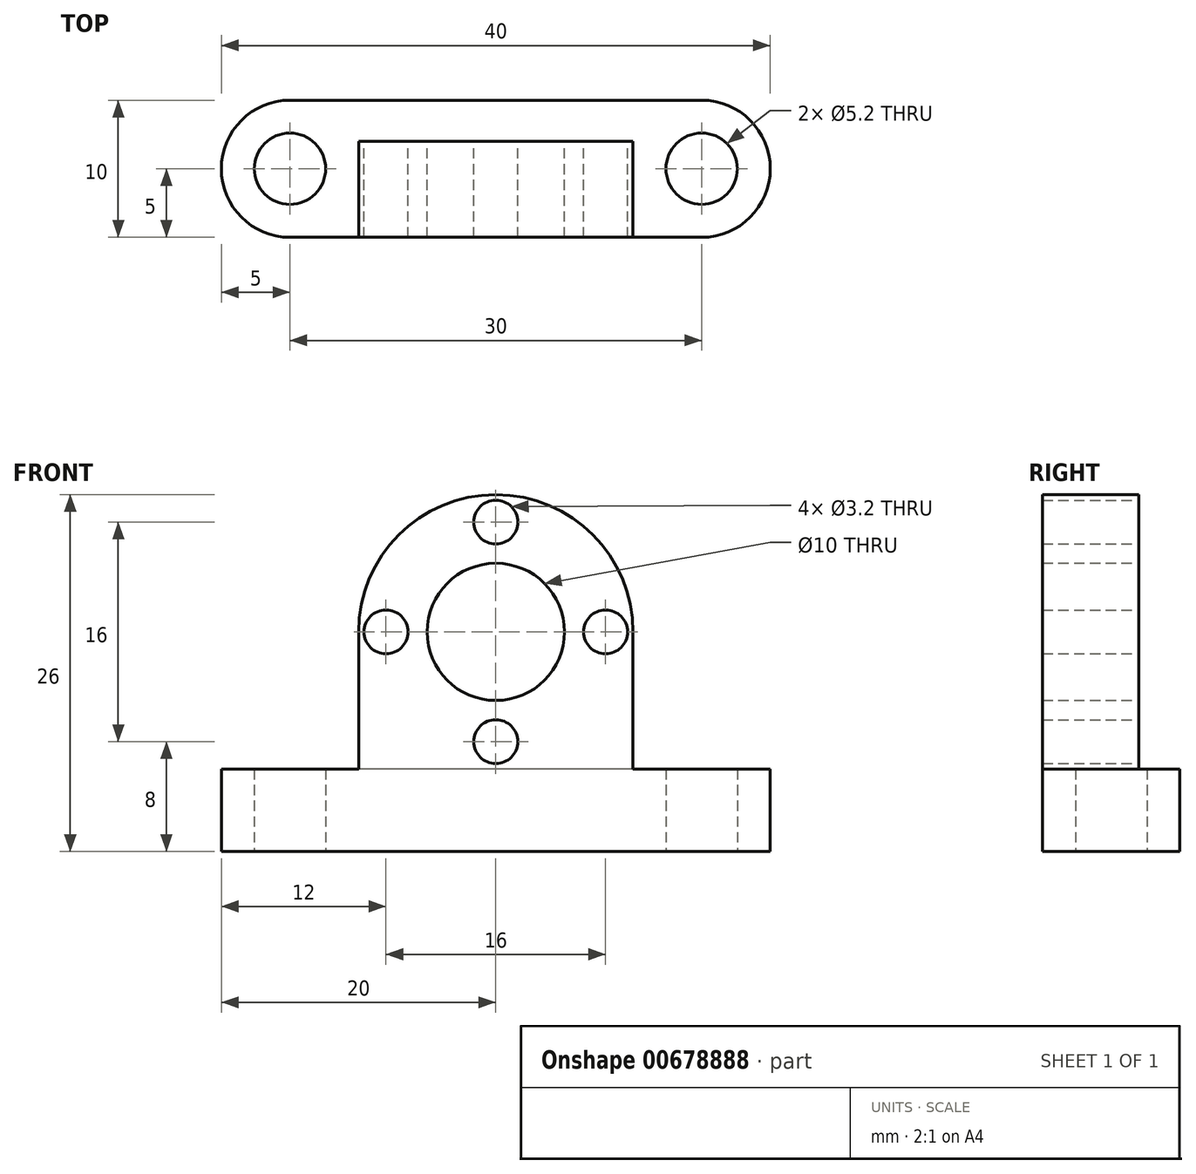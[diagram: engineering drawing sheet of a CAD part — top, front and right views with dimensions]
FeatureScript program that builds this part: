
annotation { "Feature Type Name" : "Feature", "Feature Type Description" : "" }
export const myFeature = defineFeature(function(context is Context, id is Id, definition is map)
    precondition{}
    {
        {
            var Q0;
            Q0=qCreatedBy(makeId("Top.planeOp"),FACE);
            var sketch = newSketch(context, id + "F0", { "sketchPlane" : qUnion([Q0])});
            skCircle(sketch, "E0", {"center": v(-15, 0) * mm, "radius": 2.6 * mm});
            skCircle(sketch, "E1", {"center": v(15, 0) * mm, "radius": 2.6 * mm});
            skLineSegment(sketch, "E2.bottom", {"start": v(15, -5) * mm, "end": v(-15, -5) * mm});
            skLineSegment(sketch, "E2.top", {"start": v(15, 5) * mm, "end": v(-15, 5) * mm});
            skLineSegment(sketch, "E2.left", {"start": v(20, 0) * mm, "end": v(20, 0) * mm});
            skLineSegment(sketch, "E2.right", {"start": v(-20, 0) * mm, "end": v(-20, 0) * mm});
            skPoint(sketch, "E2.middle", {"position": v(0, 0) * mm});
            skLineSegment(sketch, "E3.bottom", {"start": v(0, 0) * mm, "end": v(0, 0) * mm});
            skLineSegment(sketch, "E3.top", {"start": v(0, 0) * mm, "end": v(0, 0) * mm});
            skLineSegment(sketch, "E3.left", {"start": v(0, 0) * mm, "end": v(0, 0) * mm});
            skLineSegment(sketch, "E3.right", {"start": v(0, 0) * mm, "end": v(0, 0) * mm});
            skPoint(sketch, "E4.visualSharp", {"position": v(-20, 5) * mm});
            skArc(sketch, "E4.filletArc", {"start": v(-15, 5) * mm, "mid": v(-18.54, 3.54) * mm, "end": v(-20, 0) * mm});
            skPoint(sketch, "E5.visualSharp", {"position": v(-20, -5) * mm});
            skArc(sketch, "E5.filletArc", {"start": v(-20, 0) * mm, "mid": v(-18.54, -3.54) * mm, "end": v(-15, -5) * mm});
            skPoint(sketch, "E6.visualSharp", {"position": v(20, -5) * mm});
            skArc(sketch, "E6.filletArc", {"start": v(15, -5) * mm, "mid": v(18.54, -3.54) * mm, "end": v(20, 0) * mm});
            skPoint(sketch, "E7.visualSharp", {"position": v(20, 5) * mm});
            skArc(sketch, "E7.filletArc", {"start": v(20, 0) * mm, "mid": v(18.54, 3.54) * mm, "end": v(15, 5) * mm});
            skSolve(sketch);
        }
        {
            var Q0;
            Q0 = qSketchRegion(id + "F0", true);
            extrude(context, id + "F1", {"entities" : qUnion([Q0]), "depth" : 6 * mm, "offsetDistance" : 25.4 * mm});
        }
        {
            var Q0;
            Q0=qCreatedBy(makeId("Front.planeOp"),FACE);
            var sketch = newSketch(context, id + "F2", { "sketchPlane" : qUnion([Q0])});
            skCircle(sketch, "E8", {"center": v(0, 16) * mm, "radius": 5 * mm});
            skArc(sketch, "E9", {"start": v(10, 16) * mm, "mid": v(0, 26) * mm, "end": v(-10, 16) * mm});
            skLineSegment(sketch, "E10", {"start": v(-10, 16) * mm, "end": v(-10, 6) * mm});
            skLineSegment(sketch, "E11", {"start": v(10, 16) * mm, "end": v(10, 6) * mm});
            skLineSegment(sketch, "E12", {"start": v(10, 6) * mm, "end": v(-10, 6) * mm});
            skSolve(sketch);
        }
        {
            var Q0;
            Q0 = qSketchRegion(id + "F2", true);
            extrude(context, id + "F3", {"entities" : qUnion([Q0]), "operationType" : NewBodyOperationType.ADD, "depth" : 5 * mm, "offsetDistance" : 25.4 * mm, "hasSecondDirection" : true, "secondDirectionOppositeDirection" : true, "secondDirectionDepth" : 2 * mm});
        }
        {
            var Q0;
            Q0=makeQuery(id+"F3.opExtrude","CAP_FACE",FACE,{"disambiguationData":[OSD([sQuery(id+"F2.wireOp",EDGE,"E8"),sQuery(id+"F2.wireOp",EDGE,"E9"),sQuery(id+"F2.wireOp",EDGE,"E10"),sQuery(id+"F2.wireOp",EDGE,"E11"),sQuery(id+"F2.wireOp",EDGE,"E12")])],"isStart":true});
            var sketch = newSketch(context, id + "F4", { "sketchPlane" : qUnion([Q0])});
            skCircle(sketch, "E13", {"center": v(0, 24) * mm, "radius": 1.6 * mm});
            skCircle(sketch, "E14", {"center": v(8, 16) * mm, "radius": 1.6 * mm});
            skCircle(sketch, "E15", {"center": v(0, 8) * mm, "radius": 1.6 * mm});
            skCircle(sketch, "E16", {"center": v(-8, 16) * mm, "radius": 1.6 * mm});
            skSolve(sketch);
        }
        {
            var Q0;
            Q0 = qSketchRegion(id + "F4", true);
            extrude(context, id + "F5", {"entities" : qUnion([Q0]), "operationType" : NewBodyOperationType.REMOVE, "endBound" : BoundingType.THROUGH_ALL, "oppositeDirection" : true, "depth" : 25.4 * mm, "offsetDistance" : 25.4 * mm});
        }
    });
